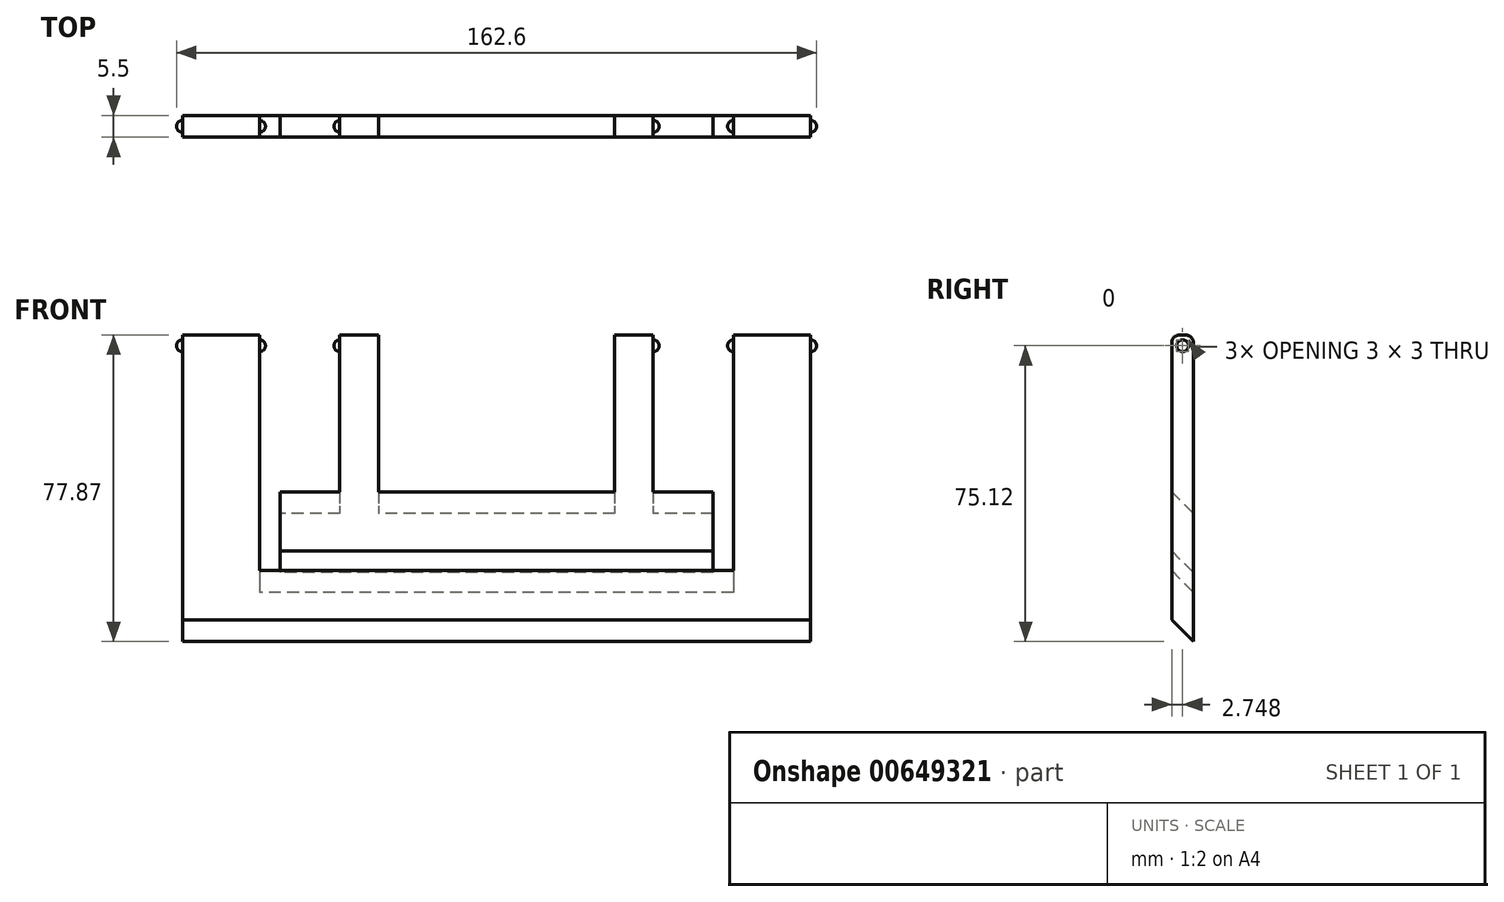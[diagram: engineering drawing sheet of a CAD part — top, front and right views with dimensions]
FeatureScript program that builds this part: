
annotation { "Feature Type Name" : "Feature", "Feature Type Description" : "" }
export const myFeature = defineFeature(function(context is Context, id is Id, definition is map)
    precondition{}
    {
        {
            var Q0;
            Q0=qCreatedBy(makeId("Right.planeOp"),FACE);
            var sketch = newSketch(context, id + "F0", { "sketchPlane" : qUnion([Q0])});
            skLineSegment(sketch, "E0", {"start": v(0.02, 88) * mm, "end": v(0.02, 2) * mm, "construction": true});
            skLineSegment(sketch, "E1", {"start": v(-1.98, 0) * mm, "end": v(-15.36, 0) * mm, "construction": true});
            skLineSegment(sketch, "E2", {"start": v(-5.36, 43.95) * mm, "end": v(-5.36, 88) * mm, "construction": true});
            skLineSegment(sketch, "E3", {"start": v(-3.36, 90) * mm, "end": v(-1.98, 90) * mm, "construction": true});
            skPoint(sketch, "E4.visualSharp", {"position": v(0.78, 9.5) * mm});
            skPoint(sketch, "E5.visualSharp", {"position": v(-11.22, 10.5) * mm});
            skPoint(sketch, "E6.visualSharp", {"position": v(-11.22, 3.5) * mm});
            skArc(sketch, "E6.filletArc", {"start": v(-17.36, 2) * mm, "mid": v(-16.78, 0.59) * mm, "end": v(-15.36, 0) * mm, "construction": true});
            skPoint(sketch, "E7.visualSharp", {"position": v(6.78, 3.5) * mm});
            skArc(sketch, "E7.filletArc", {"start": v(-1.98, 0) * mm, "mid": v(-0.56, 0.59) * mm, "end": v(0.02, 2) * mm, "construction": true});
            skPoint(sketch, "E8.visualSharp", {"position": v(6.28, 93.5) * mm});
            skArc(sketch, "E8.filletArc", {"start": v(0.02, 88) * mm, "mid": v(-0.56, 89.41) * mm, "end": v(-1.98, 90) * mm, "construction": true});
            skPoint(sketch, "E9.visualSharp", {"position": v(0.78, 93.5) * mm});
            skArc(sketch, "E9.filletArc", {"start": v(-3.36, 90) * mm, "mid": v(-4.78, 89.41) * mm, "end": v(-5.36, 88) * mm, "construction": true});
            skLineSegment(sketch, "E10", {"start": v(-9.7, 6.36) * mm, "end": v(-16.28, 6.9) * mm, "construction": true});
            skLineSegment(sketch, "E11", {"start": v(-17.36, 2) * mm, "end": v(-17.36, 5.91) * mm, "construction": true});
            skArc(sketch, "E12.filletArc", {"start": v(-16.28, 6.9) * mm, "mid": v(-17.04, 6.65) * mm, "end": v(-17.36, 5.91) * mm, "construction": true});
            skLineSegment(sketch, "E13", {"start": v(-5.36, 43.95) * mm, "end": v(-5.36, 9.26) * mm, "construction": true});
            skLineSegment(sketch, "E14", {"start": v(-9.7, 6.36) * mm, "end": v(-8.61, 6.27) * mm, "construction": true});
            skArc(sketch, "E15.filletArc", {"start": v(-8.61, 6.27) * mm, "mid": v(-6.33, 7.05) * mm, "end": v(-5.36, 9.26) * mm, "construction": true});
            skCircle(sketch, "E16", {"center": v(-4, 4) * mm, "radius": 2.75 * mm, "construction": true});
            skLineSegment(sketch, "E17", {"start": v(-11.3, 80) * mm, "end": v(-11.3, 15.94) * mm, "construction": true});
            skLineSegment(sketch, "E18", {"start": v(-11.3, 15.94) * mm, "end": v(-1.98, 5.87) * mm, "construction": true});
            skLineSegment(sketch, "E19", {"start": v(-16.4, 13.36) * mm, "end": v(-6.02, 2.13) * mm, "construction": true});
            skLineSegment(sketch, "E20", {"start": v(-16.4, 80) * mm, "end": v(-16.4, 13.36) * mm, "construction": true});
            skLineSegment(sketch, "E21", {"start": v(-1.98, 5.87) * mm, "end": v(-6.02, 2.13) * mm, "construction": true});
            skLineSegment(sketch, "E22", {"start": v(-5.4, 80) * mm, "end": v(-5.4, 18.04) * mm});
            skLineSegment(sketch, "E23", {"start": v(-10.9, 17.63) * mm, "end": v(-10.9, 80) * mm});
            skLineSegment(sketch, "E24", {"start": v(-10.9, 17.63) * mm, "end": v(-5.4, 12.13) * mm});
            skLineSegment(sketch, "E25", {"start": v(-5.4, 12.13) * mm, "end": v(-5.4, 18.04) * mm});
            skLineSegment(sketch, "E26", {"start": v(-16.4, 80) * mm, "end": v(-16.4, 88) * mm, "construction": true});
            skLineSegment(sketch, "E27", {"start": v(-14.4, 90) * mm, "end": v(-7.5, 90) * mm, "construction": true});
            skLineSegment(sketch, "E28", {"start": v(-5.5, 88) * mm, "end": v(-5.5, 86.5) * mm, "construction": true});
            skLineSegment(sketch, "E29", {"start": v(-7.5, 84.5) * mm, "end": v(-9.5, 84.5) * mm, "construction": true});
            skLineSegment(sketch, "E30", {"start": v(-11.3, 82.5) * mm, "end": v(-11.3, 80) * mm, "construction": true});
            skPoint(sketch, "E31.visualSharp", {"position": v(-16.4, 90) * mm});
            skArc(sketch, "E31.filletArc", {"start": v(-14.4, 90) * mm, "mid": v(-15.82, 89.41) * mm, "end": v(-16.4, 88) * mm, "construction": true});
            skPoint(sketch, "E32.visualSharp", {"position": v(-5.5, 90) * mm});
            skArc(sketch, "E32.filletArc", {"start": v(-5.5, 88) * mm, "mid": v(-6.09, 89.41) * mm, "end": v(-7.5, 90) * mm, "construction": true});
            skPoint(sketch, "E33.visualSharp", {"position": v(-5.5, 84.5) * mm});
            skArc(sketch, "E33.filletArc", {"start": v(-7.5, 84.5) * mm, "mid": v(-6.09, 85.09) * mm, "end": v(-5.5, 86.5) * mm, "construction": true});
            skPoint(sketch, "E34.visualSharp", {"position": v(-11.3, 84.5) * mm});
            skLineSegment(sketch, "E35", {"start": v(-9.5, 84.5) * mm, "end": v(-11.3, 84.5) * mm, "construction": true});
            skLineSegment(sketch, "E36", {"start": v(-11.3, 82.5) * mm, "end": v(-11.3, 84.5) * mm, "construction": true});
            skLineSegment(sketch, "E37", {"start": v(-10.9, 80) * mm, "end": v(-10.9, 88) * mm});
            skLineSegment(sketch, "E38", {"start": v(-8.9, 90) * mm, "end": v(-7.4, 90) * mm});
            skLineSegment(sketch, "E39", {"start": v(-5.4, 88) * mm, "end": v(-5.4, 80) * mm});
            skPoint(sketch, "E40.visualSharp", {"position": v(-10.9, 90) * mm});
            skArc(sketch, "E40.filletArc", {"start": v(-8.9, 90) * mm, "mid": v(-10.32, 89.41) * mm, "end": v(-10.9, 88) * mm});
            skPoint(sketch, "E41.visualSharp", {"position": v(-5.4, 90) * mm});
            skArc(sketch, "E41.filletArc", {"start": v(-5.4, 88) * mm, "mid": v(-5.99, 89.41) * mm, "end": v(-7.4, 90) * mm});
            skLineSegment(sketch, "E42", {"start": v(-10.9, 30.13) * mm, "end": v(-5.4, 24.63) * mm});
            skLineSegment(sketch, "E43", {"start": v(-10.9, 30.13) * mm, "end": v(-10.9, 88) * mm});
            skLineSegment(sketch, "E44", {"start": v(-5.4, 88) * mm, "end": v(-5.4, 24.63) * mm});
            skLineSegment(sketch, "E45", {"start": v(-10.9, 35.13) * mm, "end": v(-5.4, 29.63) * mm});
            skLineSegment(sketch, "E46", {"start": v(-10.9, 50.13) * mm, "end": v(-5.4, 44.63) * mm});
            skSolve(sketch);
        }
        {
            var Q0;
            Q0 = qSketchRegion(id + "F0", true);
            extrude(context, id + "F1", {"entities" : qUnion([Q0]), "depth" : 79.8 * mm, "offsetDistance" : 25 * mm, "hasSecondDirection" : true, "secondDirectionOppositeDirection" : true, "secondDirectionDepth" : 79.8 * mm});
        }
        {
            var Q0;
            {var subQ0=sQuery(id+"F0.wireOp",EDGE,"E42");Q0=makeQuery(id+"F0.imprint","IMPRINT",FACE,{"disambiguationData":[TD([[makeQuery(id+"F0.imprint","IMPRINT",EDGE,{"derivedFrom":subQ0}),1.0]])]});}
            var Q1;
            {var subQ0=sQuery(id+"F0.wireOp",EDGE,"E45");Q1=makeQuery(id+"F0.imprint","IMPRINT",FACE,{"disambiguationData":[TD([[makeQuery(id+"F0.imprint","IMPRINT",EDGE,{"derivedFrom":subQ0}),1.0]])]});}
            var Q2;
            Q2=makeQuery(id+"F0.imprint","IMPRINT",FACE,{"disambiguationData":[TD([[makeQuery(id+"F0.imprint","IMPRINT",EDGE,{"derivedFrom":sQuery(id+"F0.wireOp",EDGE,"E38")}),-1.0]])]});
            extrude(context, id + "F2", {"entities" : qUnion([Q0, Q1, Q2]), "operationType" : NewBodyOperationType.REMOVE, "depth" : 60.2 * mm, "offsetDistance" : 25 * mm, "hasSecondDirection" : true, "secondDirectionOppositeDirection" : true, "secondDirectionDepth" : 60.2 * mm});
        }
        {
            var Q0;
            {var subQ0=sQuery(id+"F0.wireOp",EDGE,"E45");Q0=makeQuery(id+"F0.imprint","IMPRINT",FACE,{"disambiguationData":[TD([[makeQuery(id+"F0.imprint","IMPRINT",EDGE,{"derivedFrom":subQ0}),1.0]])]});}
            extrude(context, id + "F3", {"entities" : qUnion([Q0]), "depth" : 55 * mm, "offsetDistance" : 25 * mm, "hasSecondDirection" : true, "secondDirectionOppositeDirection" : true, "secondDirectionDepth" : 55 * mm});
        }
        {
            var Q0;
            Q0=makeQuery(id+"F0.imprint","IMPRINT",FACE,{"disambiguationData":[TD([[makeQuery(id+"F0.imprint","IMPRINT",EDGE,{"derivedFrom":sQuery(id+"F0.wireOp",EDGE,"E38")}),-1.0]])]});
            extrude(context, id + "F4", {"entities" : qUnion([Q0]), "operationType" : NewBodyOperationType.ADD, "depth" : 39.8 * mm, "offsetDistance" : 25 * mm, "hasSecondDirection" : true, "secondDirectionOppositeDirection" : true, "secondDirectionDepth" : 39.8 * mm});
        }
        {
            var Q0;
            Q0=makeQuery(id+"F0.imprint","IMPRINT",FACE,{"disambiguationData":[TD([[makeQuery(id+"F0.imprint","IMPRINT",EDGE,{"derivedFrom":sQuery(id+"F0.wireOp",EDGE,"E38")}),-1.0]])]});
            extrude(context, id + "F5", {"entities" : qUnion([Q0]), "operationType" : NewBodyOperationType.REMOVE, "depth" : 20.2 * mm, "offsetDistance" : 25 * mm, "hasSecondDirection" : true, "secondDirectionOppositeDirection" : true, "secondDirectionDepth" : 20.2 * mm});
        }
        {
            var Q0;
            Q0=makeQuery(id+"F1.opExtrude","CAP_FACE",FACE,{"disambiguationData":[OSD([sQuery(id+"F0.wireOp",EDGE,"E22"),sQuery(id+"F0.wireOp",EDGE,"E23"),sQuery(id+"F0.wireOp",EDGE,"E24"),sQuery(id+"F0.wireOp",EDGE,"E25"),sQuery(id+"F0.wireOp",EDGE,"E38"),sQuery(id+"F0.wireOp",EDGE,"E40.filletArc"),sQuery(id+"F0.wireOp",EDGE,"E41.filletArc"),sQuery(id+"F0.wireOp",EDGE,"E43"),sQuery(id+"F0.wireOp",EDGE,"E44")])],"isStart":true});
            var sketch = newSketch(context, id + "F6", { "sketchPlane" : qUnion([Q0])});
            skCircle(sketch, "E47", {"center": v(8.15, 87.25) * mm, "radius": 1.5 * mm});
            skSolve(sketch);
        }
        {
            var Q0;
            Q0 = qSketchRegion(id + "F6", true);
            extrude(context, id + "F7", {"entities" : qUnion([Q0]), "operationType" : NewBodyOperationType.ADD, "depth" : 1.5 * mm, "offsetDistance" : 25 * mm, "hasSecondDirection" : true, "secondDirectionOppositeDirection" : true, "secondDirectionDepth" : 21.1 * mm});
        }
        {
            var Q0;
            Q0=makeQuery(id+"F7.opExtrude","CAP_EDGE",EDGE,{"disambiguationData":[OSD([sQuery(id+"F6.wireOp",EDGE,"E47")])],"isStart":false});
            var Q1;
            Q1=makeQuery(id+"F7.opExtrude","CAP_EDGE",EDGE,{"disambiguationData":[OSD([sQuery(id+"F6.wireOp",EDGE,"E47")])],"isStart":true});
            fillet(context, id + "F8", {"entities" : qUnion([Q0, Q1]), "radius" : 1.5 * mm, "tangentPropagation" : true, "allowEdgeOverflow" : false});
        }
        {
            var Q0;
            Q0=makeQuery(id+"F4.opExtrude","CAP_FACE",FACE,{"disambiguationData":[OSD([sQuery(id+"F0.wireOp",EDGE,"E38"),sQuery(id+"F0.wireOp",EDGE,"E40.filletArc"),sQuery(id+"F0.wireOp",EDGE,"E41.filletArc"),sQuery(id+"F0.wireOp",EDGE,"E43"),sQuery(id+"F0.wireOp",EDGE,"E44"),sQuery(id+"F0.wireOp",EDGE,"E46")])],"isStart":true});
            var sketch = newSketch(context, id + "F9", { "sketchPlane" : qUnion([Q0])});
            skCircle(sketch, "E48", {"center": v(8.15, 87.25) * mm, "radius": 1.5 * mm});
            skSolve(sketch);
        }
        {
            var Q0;
            Q0 = qSketchRegion(id + "F9", true);
            extrude(context, id + "F10", {"entities" : qUnion([Q0]), "operationType" : NewBodyOperationType.ADD, "depth" : 1.5 * mm, "offsetDistance" : 25 * mm, "hasSecondDirection" : true, "secondDirectionOppositeDirection" : true, "secondDirectionDepth" : 21.1 * mm});
        }
        {
            var Q0;
            Q0=makeQuery(id+"F10.opExtrude","CAP_EDGE",EDGE,{"disambiguationData":[OSD([sQuery(id+"F9.wireOp",EDGE,"E48")])],"isStart":false});
            var Q1;
            Q1=makeQuery(id+"F10.opExtrude","CAP_EDGE",EDGE,{"disambiguationData":[OSD([sQuery(id+"F9.wireOp",EDGE,"E48")])],"isStart":true});
            fillet(context, id + "F11", {"entities" : qUnion([Q0, Q1]), "radius" : 1.5 * mm, "tangentPropagation" : true, "allowEdgeOverflow" : false});
        }
        {
            var Q0;
            Q0=makeQuery(id+"F5.boolean.opBoolean","COPY",FACE,{"derivedFrom":makeQuery(id+"F5.opExtrude","CAP_FACE",FACE,{"disambiguationData":[OSD([sQuery(id+"F0.wireOp",EDGE,"E38"),sQuery(id+"F0.wireOp",EDGE,"E40.filletArc"),sQuery(id+"F0.wireOp",EDGE,"E41.filletArc"),sQuery(id+"F0.wireOp",EDGE,"E43"),sQuery(id+"F0.wireOp",EDGE,"E44"),sQuery(id+"F0.wireOp",EDGE,"E46")])],"isStart":false})});
            var sketch = newSketch(context, id + "F12", { "sketchPlane" : qUnion([Q0])});
            skCircle(sketch, "E49", {"center": v(8.15, 87.25) * mm, "radius": 1.5 * mm});
            skSolve(sketch);
        }
        {
            var Q0;
            Q0 = qSketchRegion(id + "F12", true);
            extrude(context, id + "F13", {"entities" : qUnion([Q0]), "operationType" : NewBodyOperationType.ADD, "depth" : 1.5 * mm, "offsetDistance" : 25 * mm, "hasSecondDirection" : true, "secondDirectionOppositeDirection" : true, "secondDirectionDepth" : 21.1 * mm});
        }
        {
            var Q0;
            Q0=makeQuery(id+"F13.opExtrude","CAP_EDGE",EDGE,{"disambiguationData":[OSD([sQuery(id+"F12.wireOp",EDGE,"E49")])],"isStart":false});
            var Q1;
            Q1=makeQuery(id+"F13.opExtrude","CAP_EDGE",EDGE,{"disambiguationData":[OSD([sQuery(id+"F12.wireOp",EDGE,"E49")])],"isStart":true});
            fillet(context, id + "F14", {"entities" : qUnion([Q0, Q1]), "radius" : 1.5 * mm, "tangentPropagation" : true, "allowEdgeOverflow" : false});
        }
        {
            var Q0;
            Q0=makeQuery(id+"F2.boolean.opBoolean","COPY",FACE,{"derivedFrom":makeQuery(id+"F2.opExtrude","CAP_FACE",FACE,{"disambiguationData":[OSD([sQuery(id+"F0.wireOp",EDGE,"E38"),sQuery(id+"F0.wireOp",EDGE,"E40.filletArc"),sQuery(id+"F0.wireOp",EDGE,"E41.filletArc"),sQuery(id+"F0.wireOp",EDGE,"E42"),sQuery(id+"F0.wireOp",EDGE,"E43"),sQuery(id+"F0.wireOp",EDGE,"E44")])],"isStart":false})});
            var sketch = newSketch(context, id + "F15", { "sketchPlane" : qUnion([Q0])});
            skCircle(sketch, "E50", {"center": v(8.15, 87.25) * mm, "radius": 1.5 * mm});
            skSolve(sketch);
        }
        {
            var Q0;
            Q0 = qSketchRegion(id + "F15", true);
            extrude(context, id + "F16", {"entities" : qUnion([Q0]), "operationType" : NewBodyOperationType.ADD, "depth" : 1.5 * mm, "offsetDistance" : 25 * mm, "hasSecondDirection" : true, "secondDirectionOppositeDirection" : true, "secondDirectionDepth" : 21.1 * mm});
        }
        {
            var Q0;
            Q0=makeQuery(id+"F16.opExtrude","CAP_EDGE",EDGE,{"disambiguationData":[OSD([sQuery(id+"F15.wireOp",EDGE,"E50")])],"isStart":false});
            var Q1;
            Q1=makeQuery(id+"F16.opExtrude","CAP_EDGE",EDGE,{"disambiguationData":[OSD([sQuery(id+"F15.wireOp",EDGE,"E50")])],"isStart":true});
            fillet(context, id + "F17", {"entities" : qUnion([Q0, Q1]), "radius" : 1.5 * mm, "tangentPropagation" : true, "allowEdgeOverflow" : false});
        }
        {
            var Q0;
            Q0=makeQuery(id+"F0.imprint","IMPRINT",FACE,{"disambiguationData":[TD([[makeQuery(id+"F0.imprint","IMPRINT",EDGE,{"derivedFrom":sQuery(id+"F0.wireOp",EDGE,"E38")}),-1.0]])]});
            extrude(context, id + "F18", {"entities" : qUnion([Q0]), "operationType" : NewBodyOperationType.REMOVE, "oppositeDirection" : true, "depth" : 30 * mm, "offsetDistance" : 25 * mm, "hasSecondDirection" : true, "secondDirectionOppositeDirection" : false, "secondDirectionDepth" : 30 * mm});
        }
    });
